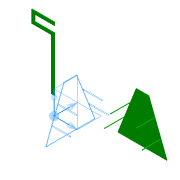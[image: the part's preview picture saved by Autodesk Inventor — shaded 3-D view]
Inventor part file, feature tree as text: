
AUTODESK INVENTOR PART (.ipt)
format: ipt  version: 2012 (Build 160160000, 160)  size: 122,368 bytes
history: native  units: in
note: dims shown in document units (in); Inventor stores cm internally (conversion verified against a paired STEP export)
features: extrude x4, sketch x4
ambient origin geometry x8: Origin, YZ Plane, XZ Plane, XY Plane, X Axis, Y Axis, Z Axis, Center Point
bodies: Solid1 (feature_tree)
feature tree (8):
  extrude  "Extrusion1"  Depth=94.0in
  extrude  "Extrusion2"  Depth=1.0in TaperAngle=0.0deg
  extrude  "Extrusion3"  Depth=30.0in
  extrude  "Extrusion4"  Depth=36.0in TaperAngle=0.0deg
  sketch  "Sketch1"  dims[d0=24.0in d1=94.0in]
  sketch  "Sketch2"  dims[d2=90.0in d3=1.0in d4=0.0in]
  sketch  "Sketch3"  dims[d5=1.5in d6=30.0in]
  sketch  "Sketch4"  dims[d7=60.0in d8=36.0in d9=0.0in d10=1.0in d11=1.0in d12=0.0in d13=6.0in d14=6.0in d15=6.0in d16=12.0in d17=104.125in d18=122.0in d19=1.0in d20=0.0in]
